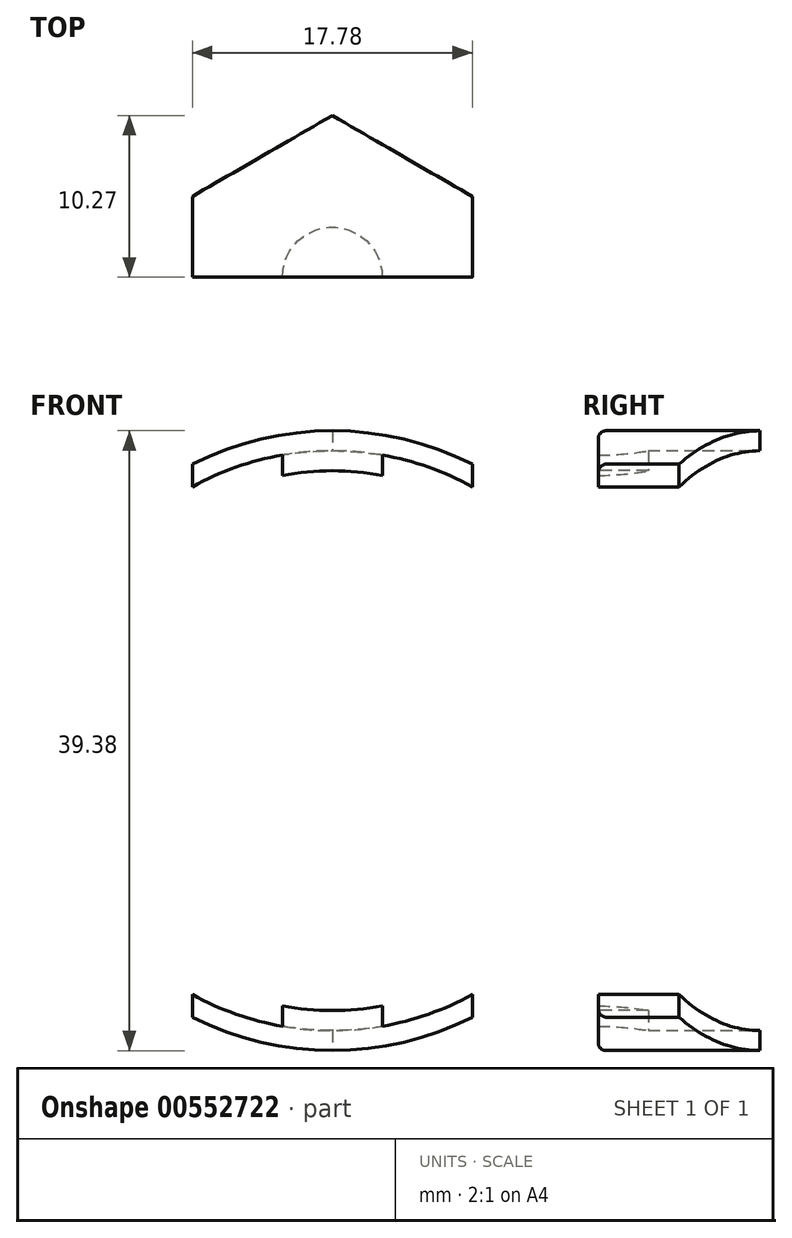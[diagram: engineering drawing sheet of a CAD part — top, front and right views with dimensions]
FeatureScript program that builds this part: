
annotation { "Feature Type Name" : "Feature", "Feature Type Description" : "" }
export const myFeature = defineFeature(function(context is Context, id is Id, definition is map)
    precondition{}
    {
        {
            var Q0;
            Q0=qCreatedBy(makeId("Front.planeOp"),FACE);
            var sketch = newSketch(context, id + "F0", { "sketchPlane" : qUnion([Q0])});
            skCircle(sketch, "E0", {"center": v(0, 0) * mm, "radius": 19.69 * mm});
            skCircle(sketch, "E1", {"center": v(0, 0) * mm, "radius": 18.41 * mm});
            skSolve(sketch);
        }
        {
            var Q0;
            Q0=qSketchRegion(id+"F0",true);
            extrude(context, id + "F1", {"entities" : qUnion([Q0]), "endBound" : BoundingType.SYMMETRIC, "depth" : 25.4 * mm, "offsetDistance" : 25.4 * mm});
        }
        {
            var Q0;
            Q0=qCreatedBy(makeId("Top.planeOp"),FACE);
            var sketch = newSketch(context, id + "F2", { "sketchPlane" : qUnion([Q0])});
            skPoint(sketch, "E2.center", {"position": v(0, 0) * mm});
            skPoint(sketch, "E3.center", {"position": v(-0.67, 0) * mm});
            skPoint(sketch, "E4.cCircle.end.orphan", {"position": v(9.6, 0) * mm});
            skCircle(sketch, "E5.cCircle", {"center": v(0, 0) * mm, "radius": 10.27 * mm, "construction": true});
            skLineSegment(sketch, "E5.0", {"start": v(0, -10.27) * mm, "end": v(-8.9, -5.13) * mm});
            skLineSegment(sketch, "E5.1", {"start": v(-8.9, -5.13) * mm, "end": v(-8.9, 5.13) * mm});
            skLineSegment(sketch, "E5.2", {"start": v(-8.9, 5.13) * mm, "end": v(0, 10.27) * mm});
            skLineSegment(sketch, "E5.3", {"start": v(0, 10.27) * mm, "end": v(8.89, 5.13) * mm});
            skLineSegment(sketch, "E5.4", {"start": v(8.89, 5.13) * mm, "end": v(8.9, -5.13) * mm});
            skLineSegment(sketch, "E5.5", {"start": v(8.89, -5.13) * mm, "end": v(0, -10.27) * mm});
            skSolve(sketch);
        }
        {
            var Q0;
            Q0=qSketchRegion(id+"F2",true);
            extrude(context, id + "F3", {"entities" : qUnion([Q0]), "operationType" : NewBodyOperationType.INTERSECT, "endBound" : BoundingType.SYMMETRIC, "depth" : 50.8 * mm, "offsetDistance" : 25.4 * mm});
        }
        {
            var Q0;
            Q0=qCreatedBy(makeId("Top.planeOp"),FACE);
            var sketch = newSketch(context, id + "F4", { "sketchPlane" : qUnion([Q0])});
            skCircle(sketch, "E6", {"center": v(0, 0) * mm, "radius": 3.18 * mm});
            skSolve(sketch);
        }
        {
            var Q0;
            Q0=qSketchRegion(id+"F4",true);
            extrude(context, id + "F5", {"entities" : qUnion([Q0]), "operationType" : NewBodyOperationType.ADD, "endBound" : BoundingType.SYMMETRIC, "depth" : 38.1 * mm, "offsetDistance" : 25.4 * mm});
        }
        {
            var Q0;
            Q0=qCreatedBy(makeId("Front.planeOp"),FACE);
            var sketch = newSketch(context, id + "F6", { "sketchPlane" : qUnion([Q0])});
            skCircle(sketch, "E7", {"center": v(0, 0) * mm, "radius": 17.15 * mm});
            skSolve(sketch);
        }
        {
            var Q0;
            Q0=qSketchRegion(id+"F6",true);
            extrude(context, id + "F7", {"entities" : qUnion([Q0]), "operationType" : NewBodyOperationType.REMOVE, "endBound" : BoundingType.SYMMETRIC, "oppositeDirection" : true, "depth" : 25.4 * mm, "offsetDistance" : 25.4 * mm});
        }
        {
            var Q0;
            Q0=qCreatedBy(makeId("Front.planeOp"),FACE);
            var sketch = newSketch(context, id + "F8", { "sketchPlane" : qUnion([Q0])});
            skCircle(sketch, "E8", {"center": v(0, 0) * mm, "radius": 20.32 * mm});
            skSolve(sketch);
        }
        {
            var Q0;
            Q0=qSketchRegion(id+"F8",true);
            extrude(context, id + "F9", {"entities" : qUnion([Q0]), "operationType" : NewBodyOperationType.REMOVE, "depth" : 25.4 * mm});
        }
        {
            var Q0;
            Q0=makeQuery(id+"F3.boolean.opBoolean","INTERSECT",EDGE,{"disambiguationData":[OD(1.0)],"derivedFrom":[makeQuery(id+"F1.opExtrude","SWEPT_FACE",FACE,{"disambiguationData":[OSD([sQuery(id+"F0.wireOp",EDGE,"E0")])]}),makeQuery(id+"F3.boolean.toolComplement.opBoolean","COPY",FACE,{"derivedFrom":makeQuery(id+"F3.opExtrude","SWEPT_FACE",FACE,{"disambiguationData":[OSD([sQuery(id+"F2.wireOp",EDGE,"E5.2")])]})})]});
            var Q1;
            Q1=makeQuery(id+"F3.boolean.opBoolean","INTERSECT",EDGE,{"disambiguationData":[OD(1.0)],"derivedFrom":[makeQuery(id+"F1.opExtrude","SWEPT_FACE",FACE,{"disambiguationData":[OSD([sQuery(id+"F0.wireOp",EDGE,"E0")])]}),makeQuery(id+"F3.boolean.toolComplement.opBoolean","COPY",FACE,{"derivedFrom":makeQuery(id+"F3.opExtrude","SWEPT_FACE",FACE,{"disambiguationData":[OSD([sQuery(id+"F2.wireOp",EDGE,"E5.3")])]})})]});
            var Q2;
            Q2=makeQuery(id+"F3.boolean.opBoolean","INTERSECT",EDGE,{"disambiguationData":[OD(1.0)],"derivedFrom":[makeQuery(id+"F1.opExtrude","SWEPT_FACE",FACE,{"disambiguationData":[OSD([sQuery(id+"F0.wireOp",EDGE,"E0")])]}),makeQuery(id+"F3.boolean.toolComplement.opBoolean","COPY",FACE,{"derivedFrom":makeQuery(id+"F3.opExtrude","SWEPT_FACE",FACE,{"disambiguationData":[OSD([sQuery(id+"F2.wireOp",EDGE,"E5.4")])]})})]});
            var Q3;
            Q3=makeQuery(id+"F3.boolean.opBoolean","INTERSECT",EDGE,{"disambiguationData":[OD(1.0)],"derivedFrom":[makeQuery(id+"F1.opExtrude","SWEPT_FACE",FACE,{"disambiguationData":[OSD([sQuery(id+"F0.wireOp",EDGE,"E0")])]}),makeQuery(id+"F3.boolean.toolComplement.opBoolean","COPY",FACE,{"derivedFrom":makeQuery(id+"F3.opExtrude","SWEPT_FACE",FACE,{"disambiguationData":[OSD([sQuery(id+"F2.wireOp",EDGE,"E5.1")])]})})]});
            var Q4;
            Q4=makeQuery(id+"F3.boolean.opBoolean","INTERSECT",EDGE,{"disambiguationData":[OD(0.0)],"derivedFrom":[makeQuery(id+"F1.opExtrude","SWEPT_FACE",FACE,{"disambiguationData":[OSD([sQuery(id+"F0.wireOp",EDGE,"E0")])]}),makeQuery(id+"F3.boolean.toolComplement.opBoolean","COPY",FACE,{"derivedFrom":makeQuery(id+"F3.opExtrude","SWEPT_FACE",FACE,{"disambiguationData":[OSD([sQuery(id+"F2.wireOp",EDGE,"E5.3")])]})})]});
            var Q5;
            Q5=makeQuery(id+"F3.boolean.opBoolean","INTERSECT",EDGE,{"disambiguationData":[OD(0.0)],"derivedFrom":[makeQuery(id+"F1.opExtrude","SWEPT_FACE",FACE,{"disambiguationData":[OSD([sQuery(id+"F0.wireOp",EDGE,"E0")])]}),makeQuery(id+"F3.boolean.toolComplement.opBoolean","COPY",FACE,{"derivedFrom":makeQuery(id+"F3.opExtrude","SWEPT_FACE",FACE,{"disambiguationData":[OSD([sQuery(id+"F2.wireOp",EDGE,"E5.4")])]})})]});
            var Q6;
            Q6=makeQuery(id+"F3.boolean.opBoolean","INTERSECT",EDGE,{"disambiguationData":[OD(0.0)],"derivedFrom":[makeQuery(id+"F1.opExtrude","SWEPT_FACE",FACE,{"disambiguationData":[OSD([sQuery(id+"F0.wireOp",EDGE,"E0")])]}),makeQuery(id+"F3.boolean.toolComplement.opBoolean","COPY",FACE,{"derivedFrom":makeQuery(id+"F3.opExtrude","SWEPT_FACE",FACE,{"disambiguationData":[OSD([sQuery(id+"F2.wireOp",EDGE,"E5.2")])]})})]});
            var Q7;
            Q7=makeQuery(id+"F3.boolean.opBoolean","INTERSECT",EDGE,{"disambiguationData":[OD(0.0)],"derivedFrom":[makeQuery(id+"F1.opExtrude","SWEPT_FACE",FACE,{"disambiguationData":[OSD([sQuery(id+"F0.wireOp",EDGE,"E0")])]}),makeQuery(id+"F3.boolean.toolComplement.opBoolean","COPY",FACE,{"derivedFrom":makeQuery(id+"F3.opExtrude","SWEPT_FACE",FACE,{"disambiguationData":[OSD([sQuery(id+"F2.wireOp",EDGE,"E5.1")])]})})]});
            var Q8;
            Q8=makeQuery(id+"F9.boolean.opBoolean","INTERSECT",EDGE,{"derivedFrom":[makeQuery(id+"F3.boolean.opBoolean","SPLIT",FACE,{"disambiguationData":[OD(1.0)],"derivedFrom":makeQuery(id+"F1.opExtrude","SWEPT_FACE",FACE,{"disambiguationData":[OSD([sQuery(id+"F0.wireOp",EDGE,"E0")])]})}),makeQuery(id+"F9.opExtrude","CAP_FACE",FACE,{"disambiguationData":[OSD([sQuery(id+"F8.wireOp",EDGE,"E8")])],"isStart":true})]});
            var Q9;
            Q9=makeQuery(id+"F9.boolean.opBoolean","INTERSECT",EDGE,{"derivedFrom":[makeQuery(id+"F3.boolean.opBoolean","SPLIT",FACE,{"disambiguationData":[OD(0.0)],"derivedFrom":makeQuery(id+"F1.opExtrude","SWEPT_FACE",FACE,{"disambiguationData":[OSD([sQuery(id+"F0.wireOp",EDGE,"E0")])]})}),makeQuery(id+"F9.opExtrude","CAP_FACE",FACE,{"disambiguationData":[OSD([sQuery(id+"F8.wireOp",EDGE,"E8")])],"isStart":true})]});
            fillet(context, id + "F10", {"entities" : qUnion([Q0, Q1, Q2, Q3, Q4, Q5, Q6, Q7, Q8, Q9]), "radius" : 0.5 * mm, "tangentPropagation" : true, "allowEdgeOverflow" : false});
        }
    });
